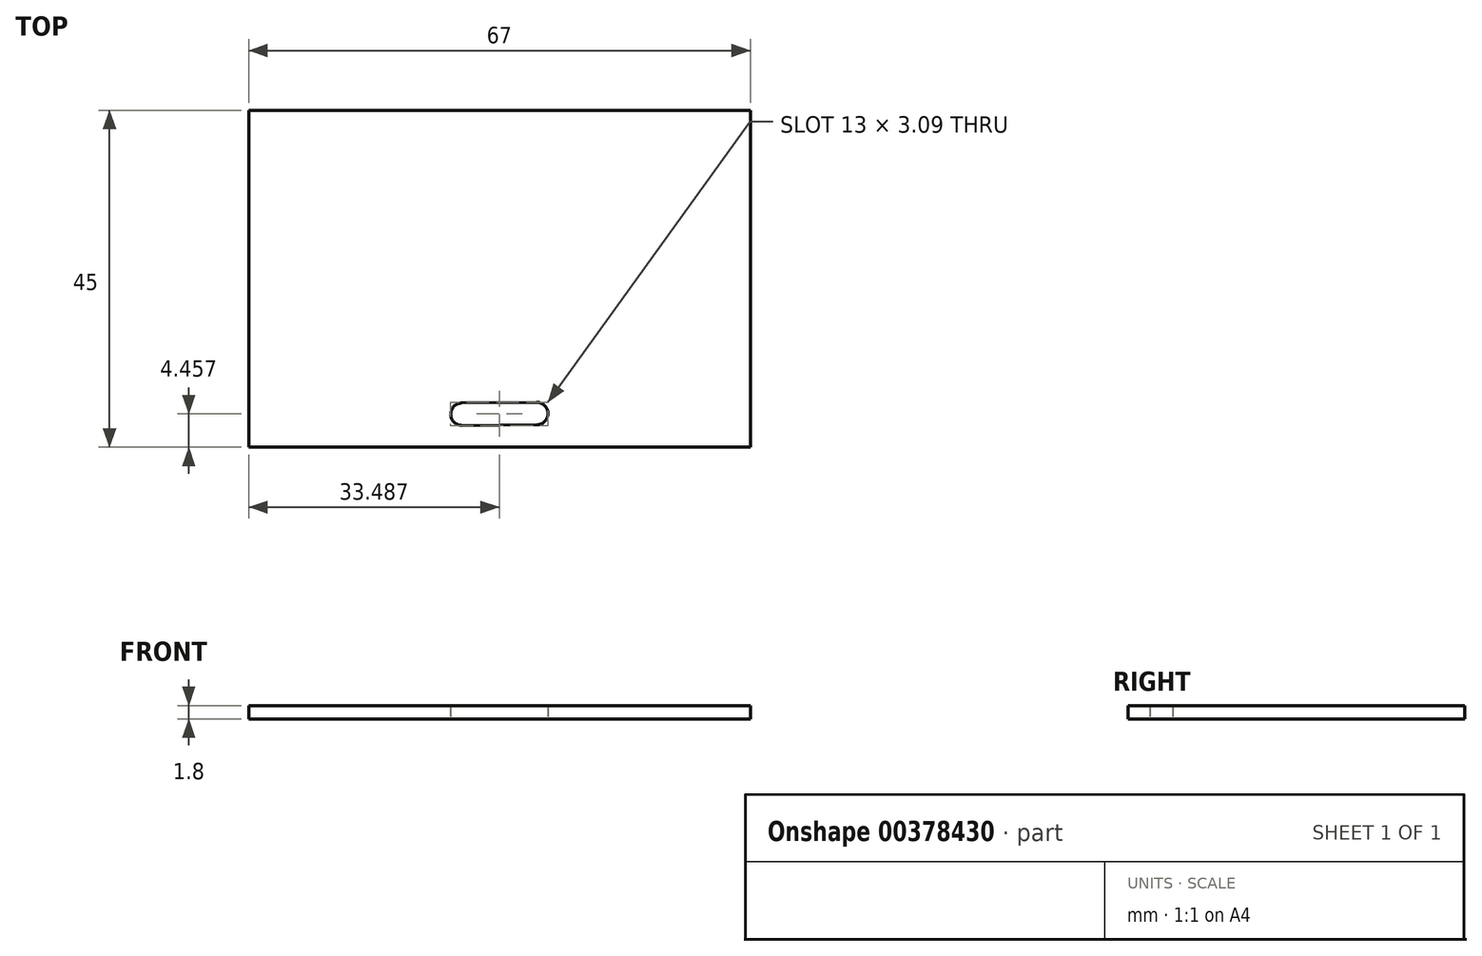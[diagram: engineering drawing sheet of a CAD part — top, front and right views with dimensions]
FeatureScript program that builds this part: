
annotation { "Feature Type Name" : "Feature", "Feature Type Description" : "" }
export const myFeature = defineFeature(function(context is Context, id is Id, definition is map)
    precondition{}
    {
        {
            var Q0;
            Q0=qCreatedBy(makeId("Top.planeOp"),FACE);
            var sketch = newSketch(context, id + "F0", { "sketchPlane" : qUnion([Q0])});
            skLineSegment(sketch, "E0.bottom", {"start": v(-33.5, 22.5) * mm, "end": v(33.5, 22.5) * mm});
            skLineSegment(sketch, "E0.top", {"start": v(-33.5, -22.5) * mm, "end": v(33.5, -22.5) * mm});
            skLineSegment(sketch, "E0.left", {"start": v(-33.5, 22.5) * mm, "end": v(-33.5, -22.5) * mm});
            skLineSegment(sketch, "E0.right", {"start": v(33.5, 22.5) * mm, "end": v(33.5, -22.5) * mm});
            skArc(sketch, "E1", {"start": v(-5.03, -16.59) * mm, "mid": v(-6.51, -18.1) * mm, "end": v(-5, -19.59) * mm});
            skArc(sketch, "E2", {"start": v(5, -19.5) * mm, "mid": v(6.49, -17.99) * mm, "end": v(4.97, -16.5) * mm});
            skLineSegment(sketch, "E3", {"start": v(-5.03, -16.59) * mm, "end": v(4.97, -16.5) * mm});
            skLineSegment(sketch, "E4", {"start": v(-5, -19.59) * mm, "end": v(5, -19.5) * mm});
            skSolve(sketch);
        }
        {
            var Q0;
            Q0=makeQuery(id+"F0.imprint","IMPRINT",FACE,{"disambiguationData":[TD([[makeQuery(id+"F0.imprint","IMPRINT",EDGE,{"derivedFrom":sQuery(id+"F0.wireOp",EDGE,"E0.bottom")}),-1.0]])]});
            extrude(context, id + "F1", {"entities" : qUnion([Q0]), "depth" : 1.8 * mm});
        }
    });
